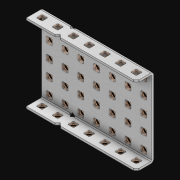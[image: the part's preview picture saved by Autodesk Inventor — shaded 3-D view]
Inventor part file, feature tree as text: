
AUTODESK INVENTOR PART (.ipt)
format: ipt  version: 2021 (Build 250183000, 183)  size: 2,975,232 bytes
history: native  units: in
note: dims shown in document units (in); Inventor stores cm internally (conversion verified against a paired STEP export)
features: extrude x50, other x49, sketch x4, thicken_offset x3, pattern_linear x3, imported_body x1
ambient origin geometry x8: Origin, YZ Plane, XZ Plane, XY Plane, X Axis, Y Axis, Z Axis, Center Point
bodies: Solid1 (feature_tree)
feature tree (110):
  thicken_offset  "Thicken1"
  thicken_offset  "Thicken2"
  thicken_offset  "Thicken3"
  pattern_linear  "Rectangular Pattern1"  Spacing1=0.001in  [1 undecoded]
  pattern_linear  "Rectangular Pattern2"  Spacing1=0.001in  [1 undecoded]
  pattern_linear  "Rectangular Pattern3"  Spacing1=0.182in  [1 undecoded]
  extrude  "Extrusion1"  Depth=0.063in TaperAngle=0.0deg
  sketch  "Sketch1"  dims[d0=0.001in]
  other  "Srf1"
  sketch  "Sketch2"  dims[d1=0.001in]
  other  "Srf2"
  sketch  "Sketch3"  dims[d2=0.001in]
  other  "Srf3"
  other  "Srf4"
  other  "Srf5"
  other  "Srf6"
  other  "Srf7"
  other  "Srf8"
  other  "Srf9"
  other  "Srf38"
  other  "Srf39"
  other  "Srf40"
  other  "Srf41"
  other  "Srf42"
  other  "Srf43"
  other  "Srf72"
  other  "Srf73"
  other  "Srf74"
  other  "Srf75"
  other  "Srf76"
  other  "Srf77"
  other  "Srf106"
  other  "Srf107"
  other  "Srf108"
  other  "Srf109"
  other  "Srf110"
  other  "Srf111"
  other  "Srf112"
  other  "Srf141"
  other  "Srf142"
  other  "Srf143"
  other  "Srf144"
  other  "Srf145"
  other  "Srf146"
  other  "Srf147"
  other  "Srf176"
  other  "Srf177"
  other  "Srf178"
  other  "Srf179"
  other  "Srf180"
  other  "Srf181"
  other  "Srf182"
  other  "Srf211"
  other  "Srf212"
  other  "Srf213"
  other  "Srf214"
  other  "Srf215"
  other  "Srf216"
  other  "Srf217"
  sketch  "Sketch4"  dims[d3=0.001in d4=0.001in d5=0.001in d6=0.182in d7=0.063in d8=0.0in d9=0.182in d10=0.063in d11=0.0in d12=0.182in d13=0.063in d14=0.0in d17=0.5in d18=2.7559in d20=0.5in d21=2.7559in d23=0.5in d24=1.9685in d26=0.5in d27=14.0in d28=0.0in]
  imported_body  "Imported1"
  extrude  "ExtrusionSrf1"  Depth=0.063in
  extrude  "ExtrusionSrf2"  Depth=0.063in TaperAngle=0.0deg
  extrude  "ExtrusionSrf3"  Depth=0.063in
  extrude  "ExtrusionSrf4"  Depth=0.063in TaperAngle=0.0deg
  extrude  "ExtrusionSrf5"  Depth=0.063in
  extrude  "ExtrusionSrf6"  Depth=0.063in
  extrude  "ExtrusionSrf7"  Depth=0.063in
  extrude  "ExtrusionSrf8"  Depth=0.063in
  extrude  "ExtrusionSrf9"  Depth=0.063in
  extrude  "ExtrusionSrf38"  Depth=0.063in
  extrude  "ExtrusionSrf39"  Depth=0.063in
  extrude  "ExtrusionSrf40"  TaperAngle=0.0deg  [1 undecoded]
  extrude  "ExtrusionSrf41"  [1 undecoded]
  extrude  "ExtrusionSrf42"  [1 undecoded]
  extrude  "ExtrusionSrf43"  [1 undecoded]
  extrude  "ExtrusionSrf72"  [1 undecoded]
  extrude  "ExtrusionSrf73"  [1 undecoded]
  extrude  "ExtrusionSrf74"  [1 undecoded]
  extrude  "ExtrusionSrf75"  [1 undecoded]
  extrude  "ExtrusionSrf76"  [1 undecoded]
  extrude  "ExtrusionSrf77"  [1 undecoded]
  extrude  "ExtrusionSrf106"  [1 undecoded]
  extrude  "ExtrusionSrf107"  [1 undecoded]
  extrude  "ExtrusionSrf108"  [1 undecoded]
  extrude  "ExtrusionSrf109"  [1 undecoded]
  extrude  "ExtrusionSrf110"  [1 undecoded]
  extrude  "ExtrusionSrf111"  [1 undecoded]
  extrude  "ExtrusionSrf112"  [1 undecoded]
  extrude  "ExtrusionSrf141"  [1 undecoded]
  extrude  "ExtrusionSrf142"  [1 undecoded]
  extrude  "ExtrusionSrf143"  [1 undecoded]
  extrude  "ExtrusionSrf144"  [1 undecoded]
  extrude  "ExtrusionSrf145"  [1 undecoded]
  extrude  "ExtrusionSrf146"  [1 undecoded]
  extrude  "ExtrusionSrf147"  [1 undecoded]
  extrude  "ExtrusionSrf176"  [1 undecoded]
  extrude  "ExtrusionSrf177"  [1 undecoded]
  extrude  "ExtrusionSrf178"  [1 undecoded]
  extrude  "ExtrusionSrf179"  [1 undecoded]
  extrude  "ExtrusionSrf180"  [1 undecoded]
  extrude  "ExtrusionSrf181"  [1 undecoded]
  extrude  "ExtrusionSrf182"  [1 undecoded]
  extrude  "ExtrusionSrf211"  [1 undecoded]
  extrude  "ExtrusionSrf212"  [1 undecoded]
  extrude  "ExtrusionSrf213"  [1 undecoded]
  extrude  "ExtrusionSrf214"  [1 undecoded]
  extrude  "ExtrusionSrf215"  [1 undecoded]
  extrude  "ExtrusionSrf216"  [1 undecoded]
  extrude  "ExtrusionSrf217"  [1 undecoded]
note: 41 required parameter values undecoded (feature->parameter linkage not recoverable at this tier; creation-order binding heuristic only, values carry confidence <= 0.55)
